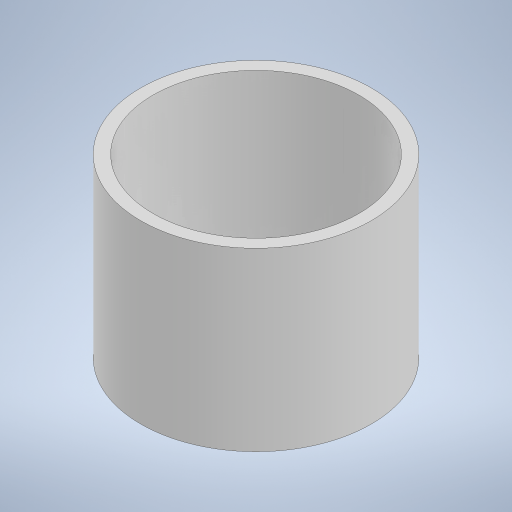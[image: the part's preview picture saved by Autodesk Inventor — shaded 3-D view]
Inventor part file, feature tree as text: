
AUTODESK INVENTOR PART (.ipt)
format: ipt  version: 2023 (Build 270158000, 158)  size: 200,192 bytes
history: native  units: in
note: dims shown in document units (in); Inventor stores cm internally (conversion verified against a paired STEP export)
features: extrude x2, sketch x1
ambient origin geometry x8: Origin, YZ Plane, XZ Plane, XY Plane, X Axis, Y Axis, Z Axis, Center Point
bodies: Solid1 (feature_tree)
feature tree (3):
  sketch  "Sketch1"  dims[d0=0.245in d1=0.2188in d2=0.1875in d3=0.0in d4=0.1562in d5=0.0in]
  extrude  "Extrusion1"  Depth=0.1562in
  extrude  "Extrusion2"  Depth=0.1875in TaperAngle=0.0deg
